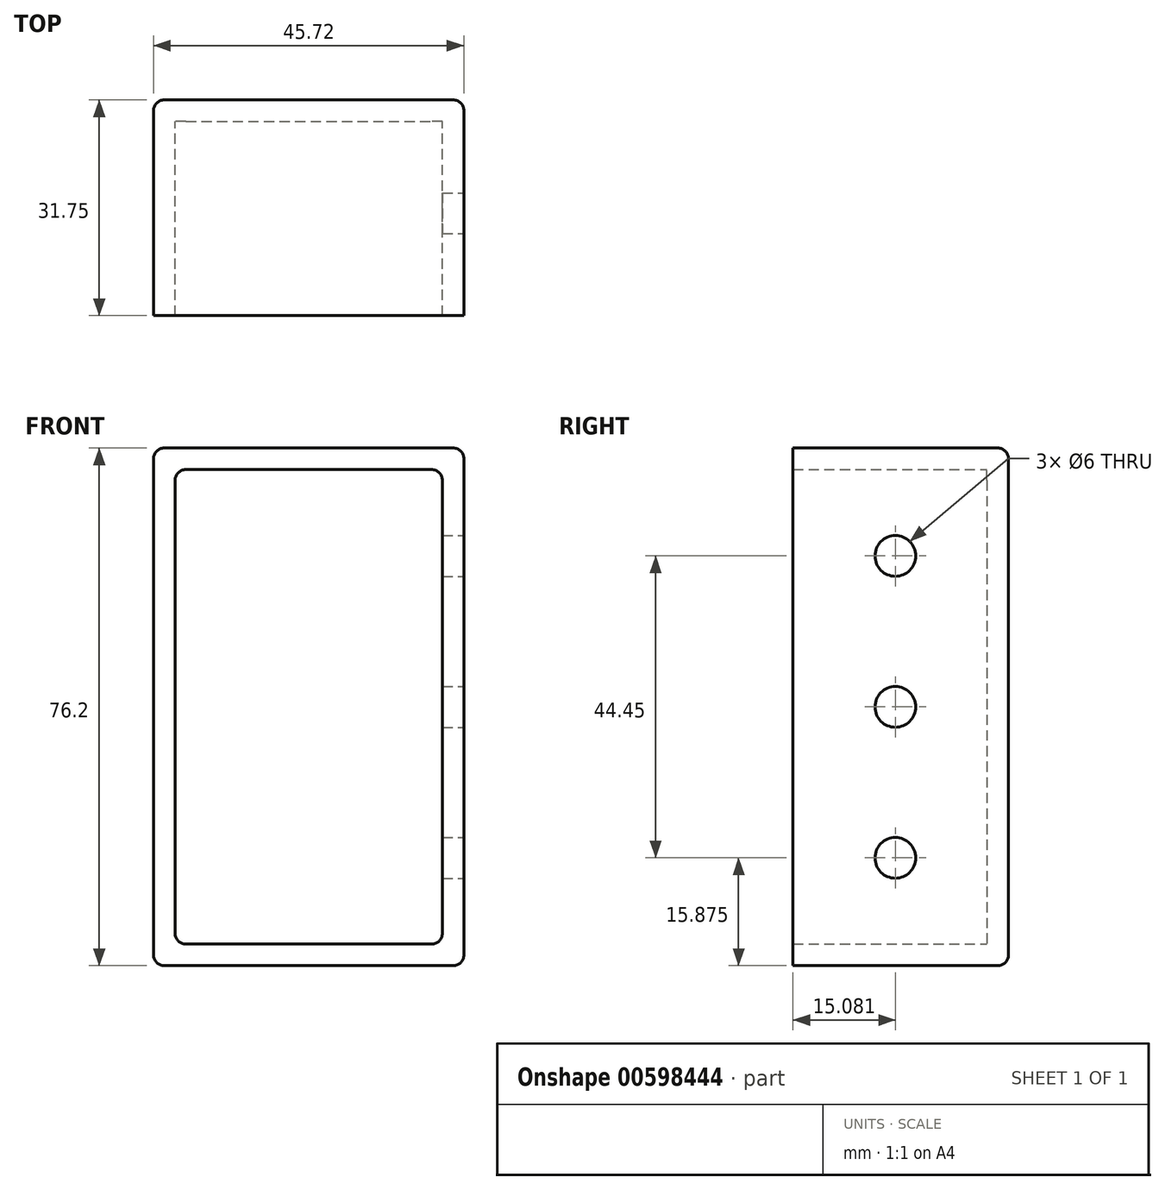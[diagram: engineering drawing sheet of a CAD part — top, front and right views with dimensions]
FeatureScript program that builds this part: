
annotation { "Feature Type Name" : "Feature", "Feature Type Description" : "" }
export const myFeature = defineFeature(function(context is Context, id is Id, definition is map)
    precondition{}
    {
        {
            var Q0;
            Q0=qCreatedBy(makeId("Front.planeOp"),FACE);
            var sketch = newSketch(context, id + "F0", { "sketchPlane" : qUnion([Q0])});
            skLineSegment(sketch, "E0.bottom", {"start": v(-21.4, 38.1) * mm, "end": v(24.32, 38.1) * mm});
            skLineSegment(sketch, "E0.top", {"start": v(-21.4, -38.1) * mm, "end": v(24.32, -38.1) * mm});
            skLineSegment(sketch, "E0.left", {"start": v(-21.4, 38.1) * mm, "end": v(-21.4, -38.1) * mm});
            skLineSegment(sketch, "E0.right", {"start": v(24.32, 38.1) * mm, "end": v(24.32, -38.1) * mm});
            skPoint(sketch, "E0.middle", {"position": v(1.46, 0) * mm});
            skLineSegment(sketch, "E1.0", {"start": v(-18.22, 34.93) * mm, "end": v(21.15, 34.93) * mm});
            skLineSegment(sketch, "E1.1", {"start": v(-18.22, 34.93) * mm, "end": v(-18.22, -34.93) * mm});
            skLineSegment(sketch, "E1.2", {"start": v(-18.22, -34.93) * mm, "end": v(21.15, -34.93) * mm});
            skLineSegment(sketch, "E1.3", {"start": v(21.15, 34.93) * mm, "end": v(21.15, -34.93) * mm});
            skSolve(sketch);
        }
        {
            var Q0;
            Q0=makeQuery(id+"F0.imprint","IMPRINT",FACE,{"disambiguationData":[TD([[makeQuery(id+"F0.imprint","IMPRINT",EDGE,{"derivedFrom":sQuery(id+"F0.wireOp",EDGE,"E0.bottom")}),-1.0]])]});
            extrude(context, id + "F1", {"entities" : qUnion([Q0]), "depth" : 31.75 * mm, "offsetDistance" : 25.4 * mm});
        }
        {
            var Q0;
            Q0=makeQuery(id+"F1.opExtrude","SWEPT_EDGE",EDGE,{"disambiguationData":[OSD([sQuery(id+"F0.wireOp",EDGE,"E0.top"),sQuery(id+"F0.wireOp",EDGE,"E0.right")])]});
            var Q1;
            Q1=makeQuery(id+"F1.opExtrude","SWEPT_EDGE",EDGE,{"disambiguationData":[OSD([sQuery(id+"F0.wireOp",EDGE,"E0.bottom"),sQuery(id+"F0.wireOp",EDGE,"E0.right")])]});
            var Q2;
            Q2=makeQuery(id+"F1.opExtrude","SWEPT_EDGE",EDGE,{"disambiguationData":[OSD([sQuery(id+"F0.wireOp",EDGE,"E0.bottom"),sQuery(id+"F0.wireOp",EDGE,"E0.left")])]});
            var Q3;
            Q3=makeQuery(id+"F1.opExtrude","SWEPT_EDGE",EDGE,{"disambiguationData":[OSD([sQuery(id+"F0.wireOp",EDGE,"E0.top"),sQuery(id+"F0.wireOp",EDGE,"E0.left")])]});
            var Q4;
            Q4=makeQuery(id+"F1.opExtrude","CAP_EDGE",EDGE,{"disambiguationData":[OSD([sQuery(id+"F0.wireOp",EDGE,"E0.left")])],"isStart":true});
            var Q5;
            Q5=makeQuery(id+"F1.opExtrude","CAP_EDGE",EDGE,{"disambiguationData":[OSD([sQuery(id+"F0.wireOp",EDGE,"E0.top")])],"isStart":true});
            var Q6;
            Q6=makeQuery(id+"F1.opExtrude","CAP_EDGE",EDGE,{"disambiguationData":[OSD([sQuery(id+"F0.wireOp",EDGE,"E0.right")])],"isStart":true});
            var Q7;
            Q7=makeQuery(id+"F1.opExtrude","CAP_EDGE",EDGE,{"disambiguationData":[OSD([sQuery(id+"F0.wireOp",EDGE,"E0.bottom")])],"isStart":true});
            fillet(context, id + "F2", {"entities" : qUnion([Q0, Q1, Q2, Q3, Q4, Q5, Q6, Q7]), "radius" : 1.59 * mm, "tangentPropagation" : true, "allowEdgeOverflow" : false});
        }
        {
            var Q0;
            Q0=makeQuery(id+"F1.opExtrude","SWEPT_FACE",FACE,{"disambiguationData":[OSD([sQuery(id+"F0.wireOp",EDGE,"E0.right")])]});
            var sketch = newSketch(context, id + "F3", { "sketchPlane" : qUnion([Q0])});
            skCircle(sketch, "E2", {"center": v(-16.67, -22.22) * mm, "radius": 3 * mm});
            skCircle(sketch, "E3", {"center": v(-16.67, 22.23) * mm, "radius": 3 * mm});
            skCircle(sketch, "E4", {"center": v(-16.67, 0) * mm, "radius": 3 * mm});
            skSolve(sketch);
        }
        {
            var Q0;
            Q0=makeQuery(id+"F0.imprint","IMPRINT",FACE,{"disambiguationData":[TD([[makeQuery(id+"F0.imprint","IMPRINT",EDGE,{"derivedFrom":sQuery(id+"F0.wireOp",EDGE,"E1.0")}),-1.0]])]});
            extrude(context, id + "F4", {"entities" : qUnion([Q0]), "operationType" : NewBodyOperationType.ADD, "depth" : 3.17 * mm, "offsetDistance" : 25.4 * mm});
        }
        {
            var Q0;
            Q0=makeQuery(id+"F1.opExtrude","SWEPT_EDGE",EDGE,{"disambiguationData":[OSD([sQuery(id+"F0.wireOp",EDGE,"E1.1"),sQuery(id+"F0.wireOp",EDGE,"E1.2")])]});
            var Q1;
            Q1=makeQuery(id+"F1.opExtrude","SWEPT_EDGE",EDGE,{"disambiguationData":[OSD([sQuery(id+"F0.wireOp",EDGE,"E1.0"),sQuery(id+"F0.wireOp",EDGE,"E1.1")])]});
            var Q2;
            Q2=makeQuery(id+"F1.opExtrude","SWEPT_EDGE",EDGE,{"disambiguationData":[OSD([sQuery(id+"F0.wireOp",EDGE,"E1.2"),sQuery(id+"F0.wireOp",EDGE,"E1.3")])]});
            var Q3;
            Q3=makeQuery(id+"F1.opExtrude","SWEPT_EDGE",EDGE,{"disambiguationData":[OSD([sQuery(id+"F0.wireOp",EDGE,"E1.0"),sQuery(id+"F0.wireOp",EDGE,"E1.3")])]});
            fillet(context, id + "F5", {"entities" : qUnion([Q0, Q1, Q2, Q3]), "radius" : 1.59 * mm, "tangentPropagation" : true, "allowEdgeOverflow" : false});
        }
        {
            var Q0;
            Q0=makeQuery(id+"F3.imprint","IMPRINT",FACE,{"disambiguationData":[TD([[makeQuery(id+"F3.imprint","IMPRINT",EDGE,{"derivedFrom":sQuery(id+"F3.wireOp",EDGE,"E2")}),1.0]])]});
            var Q1;
            Q1=makeQuery(id+"F3.imprint","IMPRINT",FACE,{"disambiguationData":[TD([[makeQuery(id+"F3.imprint","IMPRINT",EDGE,{"derivedFrom":sQuery(id+"F3.wireOp",EDGE,"E4")}),1.0]])]});
            var Q2;
            Q2=makeQuery(id+"F3.imprint","IMPRINT",FACE,{"disambiguationData":[TD([[makeQuery(id+"F3.imprint","IMPRINT",EDGE,{"derivedFrom":sQuery(id+"F3.wireOp",EDGE,"E3")}),1.0]])]});
            extrude(context, id + "F6", {"entities" : qUnion([Q0, Q1, Q2]), "operationType" : NewBodyOperationType.REMOVE, "endBound" : BoundingType.UP_TO_NEXT, "oppositeDirection" : true, "depth" : 25.4 * mm, "offsetDistance" : 25.4 * mm});
        }
    });
